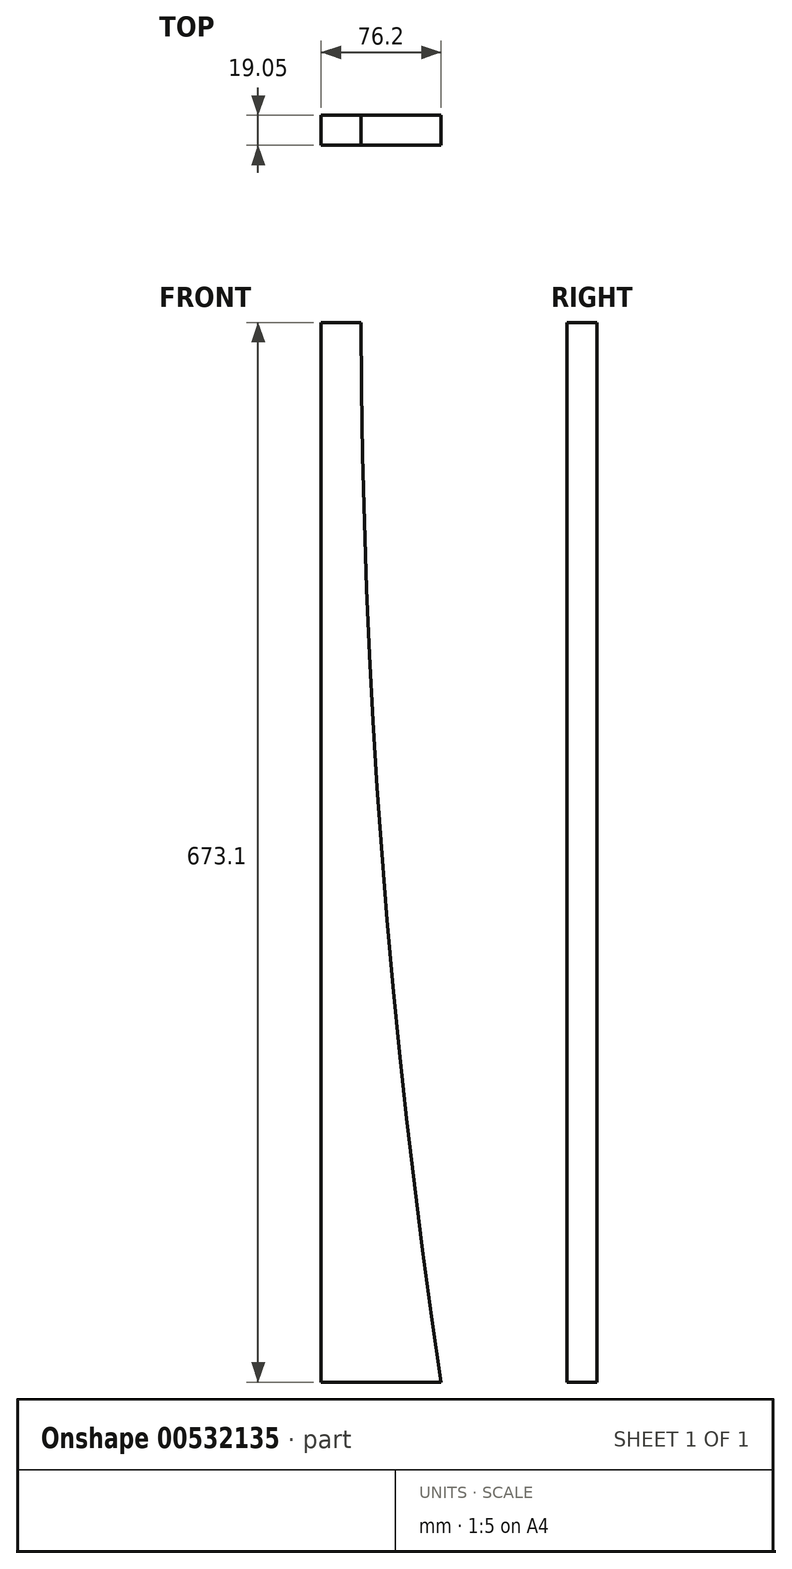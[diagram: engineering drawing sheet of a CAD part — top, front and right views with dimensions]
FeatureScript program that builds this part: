
annotation { "Feature Type Name" : "Feature", "Feature Type Description" : "" }
export const myFeature = defineFeature(function(context is Context, id is Id, definition is map)
    precondition{}
    {
        {
            var Q0;
            Q0=qCreatedBy(makeId("Front.planeOp"),FACE);
            var sketch = newSketch(context, id + "F0", { "sketchPlane" : qUnion([Q0])});
            skLineSegment(sketch, "E0", {"start": v(76.2, 0) * mm, "end": v(0, 0) * mm});
            skLineSegment(sketch, "E1", {"start": v(0, 0) * mm, "end": v(0, 673.1) * mm});
            skLineSegment(sketch, "E2", {"start": v(0, 673.1) * mm, "end": v(25.4, 673.1) * mm});
            skArc(sketch, "E3", {"start": v(25.4, 673.1) * mm, "mid": v(38.51, 335.62) * mm, "end": v(76.2, 0) * mm});
            skSolve(sketch);
        }
        {
            var Q0;
            Q0 = qSketchRegion(id + "F0", true);
            extrude(context, id + "F1", {"entities" : qUnion([Q0]), "depth" : 19.05 * mm, "offsetDistance" : 25.4 * mm});
        }
    });
